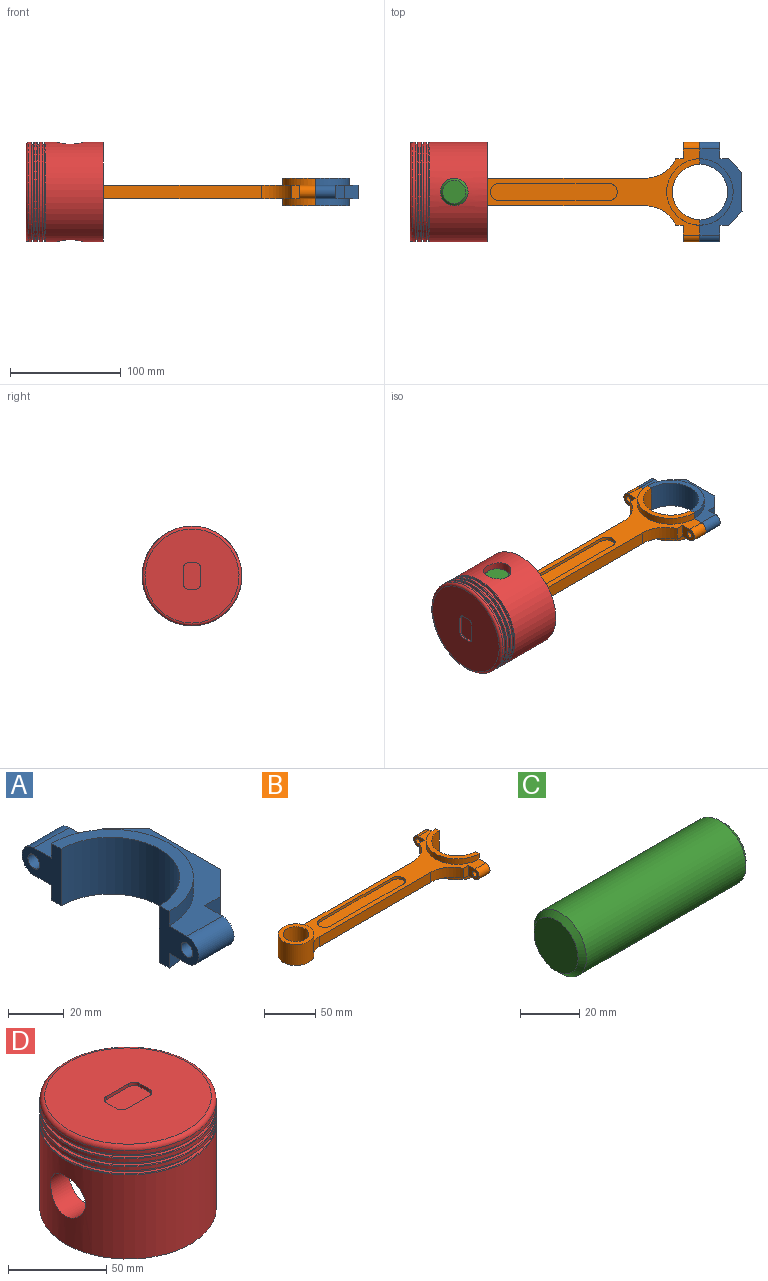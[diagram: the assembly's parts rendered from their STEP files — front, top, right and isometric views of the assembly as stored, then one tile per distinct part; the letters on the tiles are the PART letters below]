
ASSEMBLY  parts=4 mates=7
PART A: 20 faces, bbox 38x90x25 mm
  f0: plane 25x20mm, normal (-1,0,0), area 261.3mm2, adj f2,f3,f6,f7,f15,f16,f17,f18
  f1: plane 15x12mm, normal (1,0,0), area 136.3mm2, adj f2,f3,f6,f7,f12
  f2: cylinder r=6mm len=18mm, axis (-1,0,0), area 339.3mm2, adj f0,f1,f3,f6
  f3: plane 78x38mm, normal (0,0,1), area 1046.3mm2, adj f0,f1,f2,f4,f8,f9,f10,f11
  f4: cylinder r=6mm len=18mm, axis (-1,0,0), area 339.3mm2, adj f3,f6,f8,f9
  f5: cylinder r=3mm len=18mm, axis (-1,0,0), area 339.3mm2, adj f8,f9
  f6: plane 78x38mm, normal (0,0,-1), area 1046.3mm2, adj f0,f1,f2,f4,f8,f9,f10,f11
  f7: cylinder r=3mm len=18mm, axis (-1,0,0), area 339.3mm2, adj f0,f1
  f8: plane 15x12mm, normal (1,0,0), area 136.3mm2, adj f3,f4,f5,f6,f13
  f9: plane 25x20mm, normal (-1,0,0), area 261.3mm2, adj f3,f4,f5,f6,f15,f16,f17,f18
  f10: plane 36x12mm, normal (1,0,0), area 432mm2, adj f3,f6,f11,f14
  f11: plane 12x12mm, normal (0.71,0.71,0), area 203.6mm2, adj f3,f6,f10,f12
  f12: plane 12x8mm, normal (0,1,0), area 96mm2, adj f1,f3,f6,f11
  f13: plane 12x8mm, normal (0,-1,0), area 96mm2, adj f3,f6,f8,f14
  f14: plane 12x12mm, normal (0.71,-0.71,0), area 203.6mm2, adj f3,f6,f10,f13
  f15: plane 60x30mm, normal (0,0,-1), area 432mm2, adj f0,f9,f16,f17
  f16: cylinder r=30mm len=60mm, axis (0,0,-1), area 612.6mm2, adj f0,f6,f9,f15
  f17: cylinder r=25mm len=50mm, axis (0,0,-1), area 1963.5mm2, adj f0,f9,f15,f19
  f18: cylinder r=30mm len=60mm, axis (0,0,-1), area 612.6mm2, adj f0,f3,f9,f19
  f19: plane 60x30mm, normal (0,0,1), area 432mm2, adj f0,f9,f17,f18
PART B: 37 faces, bbox 239.5x90x25 mm
  f0: plane 213.48x78mm, normal (0,0,1), area 3379.3mm2, adj f1,f2,f3,f4,f5,f8,f9,f11
  f1: plane 25x20mm, normal (1,0,0), area 261.3mm2, adj f0,f10,f13,f14,f15,f16,f17,f18
  f2: plane 25x20mm, normal (1,0,0), area 261.3mm2, adj f0,f10,f13,f14,f15,f16,f17,f21
  f3: plane 12x7mm, normal (0,-1,0), area 84mm2, adj f0,f10,f12,f20
  f4: plane 12x7mm, normal (0,1,0), area 84mm2, adj f0,f10,f11,f19
  f5: cylinder r=17.5mm len=35mm, axis (0,0,-1), area 2302.8mm2, adj f0,f6,f7,f10,f35,f36
  f6: plane 35x35mm, normal (0,0,1), area 471.2mm2, adj f5,f22
  f7: plane 35x35mm, normal (0,0,-1), area 471.2mm2, adj f5,f22
  f8: plane 153.49x12mm, normal (0,1,0), area 1841.9mm2, adj f0,f10,f11,f35
  f9: plane 153.49x12mm, normal (0,-1,0), area 1841.9mm2, adj f0,f10,f12,f36
  f10: plane 213.48x78mm, normal (0,0,-1), area 3379.3mm2, adj f1,f2,f3,f4,f5,f8,f9,f11
  f11: cylinder r=30mm len=27.27mm, axis (0,0,-1), area 410.8mm2, adj f0,f4,f8,f10
  f12: cylinder r=30mm len=27.27mm, axis (0,0,-1), area 410.8mm2, adj f0,f3,f9,f10
  f13: plane 60x30mm, normal (0,0,-1), area 432mm2, adj f1,f2,f14,f15
  f14: cylinder r=25mm len=50mm, axis (0,0,-1), area 1963.5mm2, adj f1,f2,f13,f17
  f15: cylinder r=30mm len=60mm, axis (0,0,-1), area 612.6mm2, adj f1,f2,f10,f13
  f16: cylinder r=30mm len=60mm, axis (0,0,-1), area 612.6mm2, adj f0,f1,f2,f17
  f17: plane 60x30mm, normal (0,0,1), area 432mm2, adj f1,f2,f14,f16
  f18: cylinder r=6mm len=15mm, axis (1,0,0), area 282.7mm2, adj f0,f1,f10,f19
  f19: plane 15x12mm, normal (-1,0,0), area 136.3mm2, adj f0,f4,f10,f18,f24
  f20: plane 15x12mm, normal (-1,0,0), area 136.3mm2, adj f0,f3,f10,f21,f23
  f21: cylinder r=6mm len=15mm, axis (1,0,0), area 282.7mm2, adj f0,f2,f10,f20
  f22: cylinder r=12.5mm len=25mm, axis (0,0,-1), area 1963.5mm2, adj f6,f7
  f23: cylinder r=3mm len=15mm, axis (1,0,0), area 282.7mm2, adj f2,f20
  f24: cylinder r=3mm len=15mm, axis (1,0,0), area 282.7mm2, adj f1,f19
  f25: plane 100x3mm, normal (0,-1,0), area 300mm2, adj f0,f26,f28,f29
  f26: cylinder r=7.5mm len=15mm, axis (0,0,1), area 70.7mm2, adj f0,f25,f27,f29
  f27: plane 100x3mm, normal (0,1,0), area 300mm2, adj f0,f26,f28,f29
  f28: cylinder r=7.5mm len=15mm, axis (0,0,1), area 70.7mm2, adj f0,f25,f27,f29
  f29: plane 115x15mm, normal (0,0,1), area 1676.7mm2, adj f25,f26,f27,f28
  f30: cylinder r=7.5mm len=15mm, axis (0,0,-1), area 70.7mm2, adj f10,f31,f33,f34
  f31: plane 100x3mm, normal (0,-1,0), area 300mm2, adj f10,f30,f32,f34
  f32: cylinder r=7.5mm len=15mm, axis (0,0,-1), area 70.7mm2, adj f10,f31,f33,f34
  f33: plane 100x3mm, normal (0,1,0), area 300mm2, adj f10,f30,f32,f34
  f34: plane 115x15mm, normal (0,0,-1), area 1676.7mm2, adj f30,f31,f32,f33
  f35: cylinder r=22mm len=12mm, axis (0,0,-1), area 134.3mm2, adj f0,f5,f8,f10
  f36: cylinder r=22mm len=12mm, axis (0,0,-1), area 134.3mm2, adj f0,f5,f9,f10
PART C: 5 faces, bbox 80x25x25 mm
  f0: cylinder r=12.5mm len=76mm, axis (-1,0,0), area 5969mm2, adj f3,f4
  f1: plane 21x21mm, normal (1,0,0), area 346.4mm2, adj f4
  f2: plane 21x21mm, normal (-1,0,0), area 346.4mm2, adj f3
  f3: cone r=12.5mm half-angle=45deg, axis (1,0,0), area 204.4mm2, adj f0,f2
  f4: cone r=10.5mm half-angle=45deg, axis (-1,0,0), area 204.4mm2, adj f0,f1
PART D: 39 faces, bbox 97.4x97.4x70 mm
  f0: plane 85x85mm, normal (0,0,1), area 5328.2mm2, adj f23,f30,f31,f32,f33,f35,f36,f37
  f1: cylinder r=45mm len=90mm, axis (0,0,-1), area 13853.4mm2, adj f7,f21,f22,f24
  f2: cylinder r=40mm len=80mm, axis (0,0,-1), area 11847.5mm2, adj f7,f16,f18,f20
  f3: cylinder r=45mm len=90mm, axis (0,0,-1), area 640.9mm2, adj f25,f26
  f4: plane 89x89mm, normal (0,0,-1), area 412.3mm2, adj f5,f25
  f5: cylinder r=43mm len=86mm, axis (0,0,-1), area 540.4mm2, adj f4,f6
  f6: plane 89.53x89.53mm, normal (0,0,1), area 487.2mm2, adj f5,f24
  f7: plane 90x90mm, normal (0,0,-1), area 1335.2mm2, adj f1,f2
  f8: cylinder r=45mm len=90mm, axis (0,0,-1), area 640.9mm2, adj f23,f29
  f9: plane 89x89mm, normal (0,0,-1), area 412.3mm2, adj f10,f29
  f10: cylinder r=43mm len=86mm, axis (0,0,-1), area 540.4mm2, adj f9,f11
  f11: plane 89.53x89.53mm, normal (0,0,1), area 487.2mm2, adj f10,f28
  f12: cylinder r=45mm len=90mm, axis (0,0,-1), area 640.9mm2, adj f27,f28
  f13: plane 89x89mm, normal (0,0,-1), area 412.3mm2, adj f14,f27
  f14: cylinder r=43mm len=86mm, axis (0,0,-1), area 540.4mm2, adj f13,f15
  f15: plane 89.53x89.53mm, normal (0,0,1), area 487.2mm2, adj f14,f26
  f16: plane 80x80mm, normal (0,0,-1), area 5026.5mm2, adj f2
  f17: plane 35x35mm, normal (1,0,0), area 471.2mm2, adj f18,f22
  f18: cylinder r=17.5mm len=35mm, axis (1,0,0), area 880.4mm2, adj f2,f17
  f19: plane 35x35mm, normal (-1,0,0), area 471.2mm2, adj f20,f21
  f20: cylinder r=17.5mm len=35mm, axis (1,0,0), area 880.9mm2, adj f2,f19
  f21: cylinder r=12.5mm len=25mm, axis (-1,0,0), area 1108.8mm2, adj f1,f19
  f22: cylinder r=12.5mm len=25mm, axis (-1,0,0), area 1108.9mm2, adj f1,f17
  f23: torus R=42.5mm, axis (0,0,-1), area 1087.9mm2, adj f0,f8
  f24: cone r=45mm half-angle=25deg, axis (0,0,-1), area 155.6mm2, adj f1,f6
  f25: cone r=44.5mm half-angle=65deg, axis (0,0,1), area 155.1mm2, adj f3,f4
  f26: cone r=45mm half-angle=25deg, axis (0,0,-1), area 155.6mm2, adj f3,f15
  f27: cone r=44.5mm half-angle=65deg, axis (0,0,1), area 155.1mm2, adj f12,f13
  f28: cone r=45mm half-angle=25deg, axis (0,0,-1), area 155.6mm2, adj f11,f12
  f29: cone r=44.5mm half-angle=65deg, axis (0,0,1), area 155.1mm2, adj f8,f9
  f30: plane 7x2mm, normal (1,0,0), area 14mm2, adj f0,f34,f35,f38
  f31: plane 16x2mm, normal (0,1,0), area 32mm2, adj f0,f34,f35,f36
  f32: plane 7x2mm, normal (-1,0,0), area 14mm2, adj f0,f34,f36,f37
  f33: plane 16x2mm, normal (0,-1,0), area 32mm2, adj f0,f34,f37,f38
  f34: plane 24x15mm, normal (0,0,1), area 346.3mm2, adj f30,f31,f32,f33,f35,f36,f37,f38
  f35: cylinder r=4mm len=4mm, axis (0,0,1), area 12.6mm2, adj f0,f30,f31,f34
  f36: cylinder r=4mm len=4mm, axis (0,0,-1), area 12.6mm2, adj f0,f31,f32,f34
  f37: cylinder r=4mm len=4mm, axis (0,0,1), area 12.6mm2, adj f0,f32,f33,f34
  f38: cylinder r=4mm len=4mm, axis (0,0,-1), area 12.6mm2, adj f0,f30,f33,f34
PLACE A rot(axis=(0,0,1),0deg) t=(445.32,139.88,-63.62)mm
PLACE B rot(axis=(0,0,1),0deg) t=(223.32,139.88,-63.62)mm
PLACE C rot(axis=(0,-1,0),90deg) t=(223.32,139.88,-64.62)mm
PLACE D rot(axis=(0,-1,0),90deg) t=(253.32,139.88,-63.62)mm
MATE cylindrical B.f24 <-> A.f2  axis (1,0,0) through (437.82,178.88,-63.62)mm
MATE planar D.f18 <-> B.f5  axis (0,0,-1) through (223.32,139.88,-33.62)mm
MATE cylindrical B.f21 <-> A.f5  axis (1,0,0) through (445.32,100.88,-63.62)mm
MATE cylindrical D.f18 <-> C.f0  axis (0,0,-1) through (223.32,139.88,-101.18)mm
MATE planar B.f1 <-> A.f0  axis (1,0,0) through (445.32,172.07,-63.62)mm
MATE cylindrical C.f0 <-> B.f22  axis (0,0,-1) through (223.32,139.88,-64.62)mm
MATE planar D.f18 <-> C.f0  axis (0,0,-1) through (223.32,139.88,-33.62)mm
